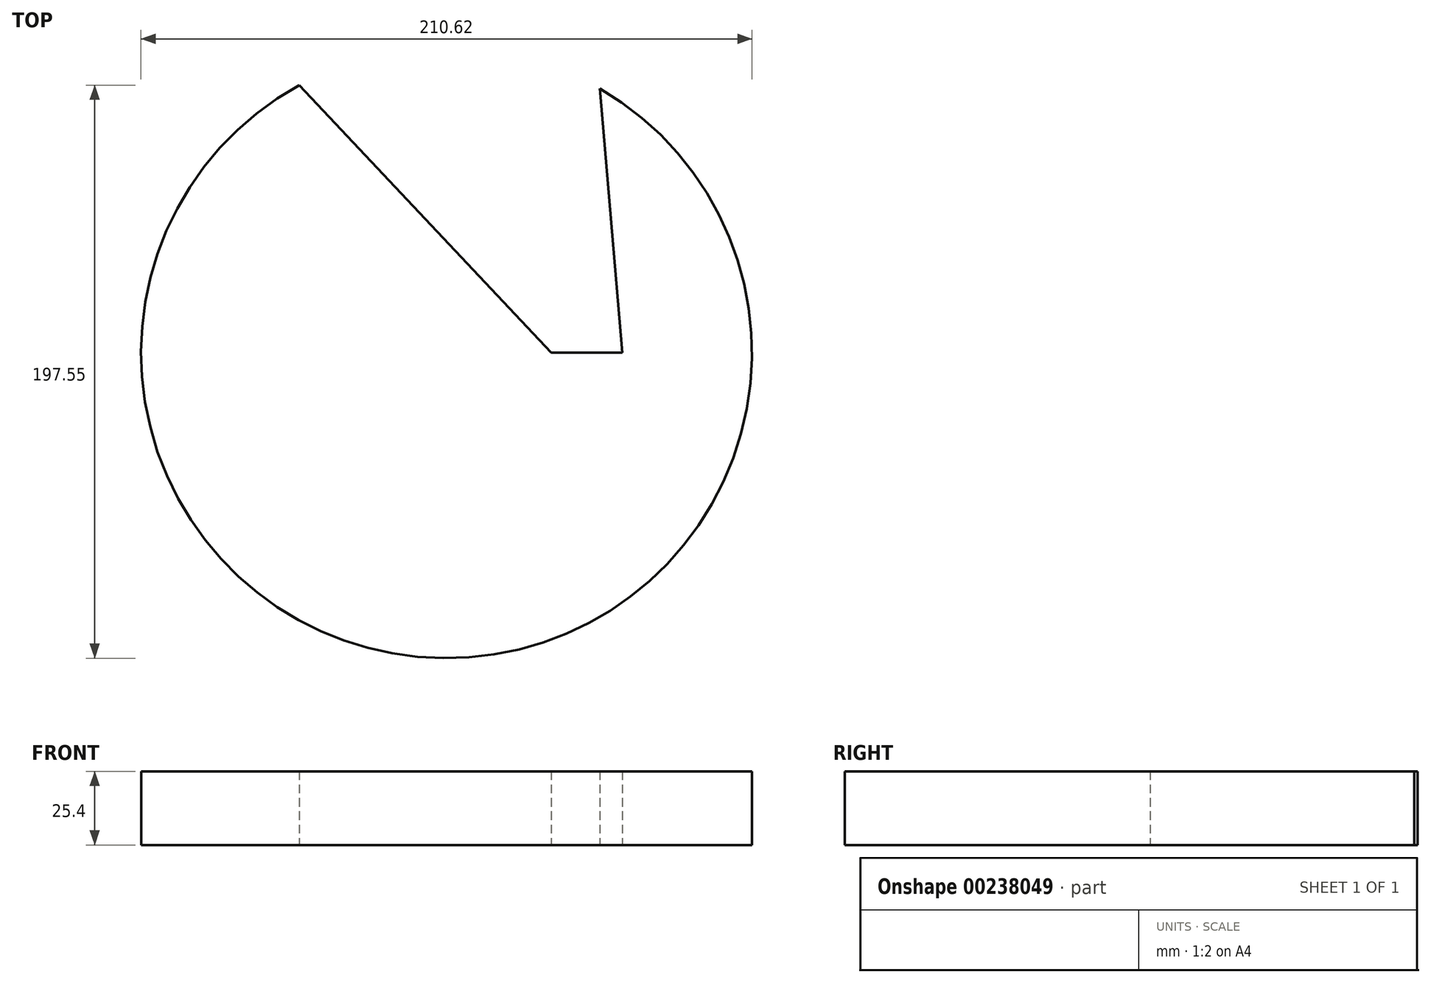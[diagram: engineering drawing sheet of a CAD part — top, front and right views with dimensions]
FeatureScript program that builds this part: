
annotation { "Feature Type Name" : "Feature", "Feature Type Description" : "" }
export const myFeature = defineFeature(function(context is Context, id is Id, definition is map)
    precondition{}
    {
        {
            var Q0;
            Q0=qCreatedBy(makeId("Top.planeOp"),FACE);
            var sketch = newSketch(context, id + "F0", { "sketchPlane" : qUnion([Q0])});
            skArc(sketch, "E0", {"start": v(-50.8, 92.24) * mm, "mid": v(-1.16, -105.3) * mm, "end": v(52.82, 91.1) * mm});
            skLineSegment(sketch, "E1", {"start": v(-50.8, 92.24) * mm, "end": v(36.14, 0) * mm});
            skLineSegment(sketch, "E2", {"start": v(36.14, 0) * mm, "end": v(60.64, 0) * mm});
            skLineSegment(sketch, "E3", {"start": v(60.64, 0) * mm, "end": v(52.82, 91.1) * mm});
            skSolve(sketch);
        }
        {
            var Q0;
            Q0 = qSketchRegion(id + "F0", true);
            extrude(context, id + "F1", {"entities" : qUnion([Q0]), "depth" : 25.4 * mm});
        }
    });
